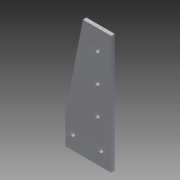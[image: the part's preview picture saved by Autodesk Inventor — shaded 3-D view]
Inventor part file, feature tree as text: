
AUTODESK INVENTOR PART (.ipt)
format: ipt  version: 2014 (Build 180170000, 170)  size: 136,704 bytes
history: native  units: in
note: dims shown in document units (in); Inventor stores cm internally (conversion verified against a paired STEP export)
features: other x3, sheet_metal_op x1, sketch x1
ambient origin geometry x8: Origin, YZ Plane, XZ Plane, XY Plane, X Axis, Y Axis, Z Axis, Center Point
bodies: Solid1 (feature_tree)
feature tree (5):
  sheet_metal_op  "Face1"
  sketch  "Sketch1"  dims[d1=4.1875in d2=0.163in d4=0.7874in d6=1.0in d7=0.3937in d9=1.0in d11=0.125in d22=0.5in d36=0.5in d37=1.5in d38=1.1811in d40=1.0in d41=0.3937in d43=1.0in d50=1.0in d51=1.0in d52=0.375in d53=1.625in d3=0.125in]
  other  "Plate1"
  other  "Definition1"
  other  "Cut1"
